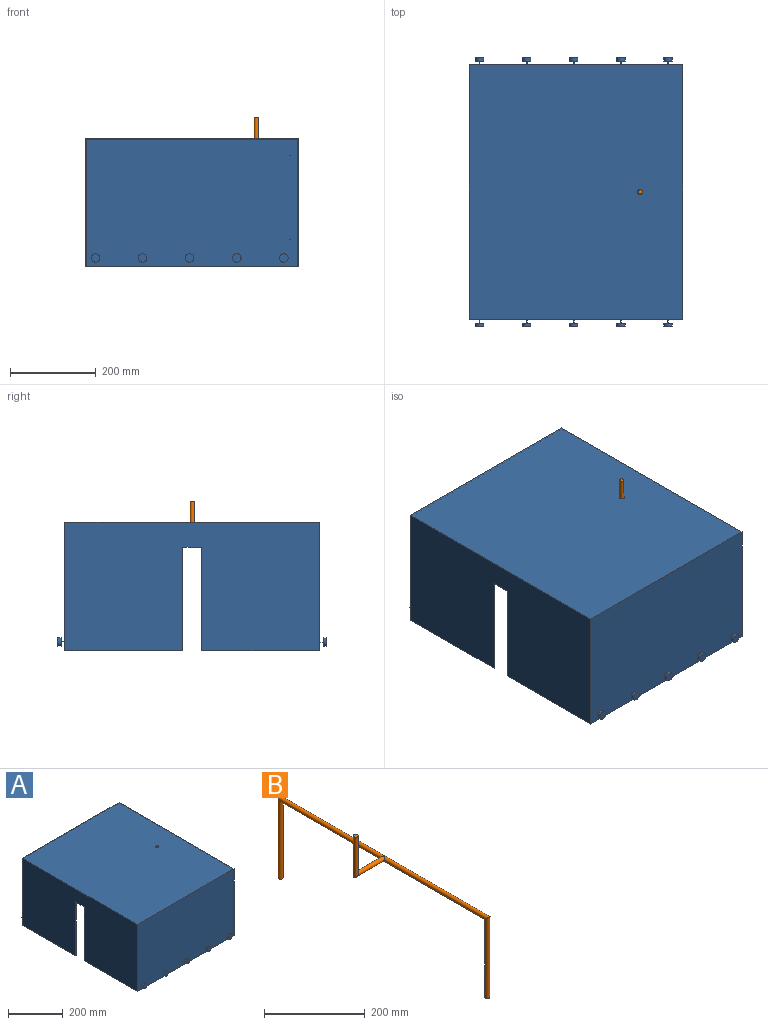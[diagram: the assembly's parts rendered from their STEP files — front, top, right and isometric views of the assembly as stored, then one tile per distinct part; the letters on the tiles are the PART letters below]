
ASSEMBLY  parts=2 mates=1
PART A: 59 faces, bbox 500x628x300 mm
  f0: plane 500x275.5mm, normal (0,0,-1), area 2615mm2, adj f4,f5,f6,f9,f10,f11,f12,f17
  f1: plane 500x275.5mm, normal (0,0,-1), area 2615mm2, adj f2,f5,f6,f7,f10,f11,f14,f15
  f2: plane 500x300mm, normal (0,1,0), area 149984.3mm2, adj f1,f3,f5,f6,f22,f26,f30,f34
  f3: plane 595x500mm, normal (0,0,1), area 297386.9mm2, adj f2,f4,f5,f6,f58
  f4: plane 500x300mm, normal (0,-1,0), area 149984.3mm2, adj f0,f3,f5,f6,f18,f42,f46,f50
  f5: plane 595x300mm, normal (-1,0,0), area 167858.5mm2, adj f0,f1,f2,f3,f4,f15,f16,f17
  f6: plane 595x300mm, normal (1,0,0), area 167858.5mm2, adj f0,f1,f2,f3,f4,f12,f13,f14
  f7: plane 495x297.5mm, normal (0,-1,0), area 147262.5mm2, adj f1,f8,f10,f11
  f8: plane 590x495mm, normal (0,0,-1), area 291936.9mm2, adj f7,f9,f10,f11,f58
  f9: plane 495x297.5mm, normal (0,1,0), area 147262.5mm2, adj f0,f8,f10,f11
  f10: plane 590x297.5mm, normal (1,0,0), area 164883.5mm2, adj f0,f1,f7,f8,f9,f15,f16,f17
  f11: plane 590x297.5mm, normal (-1,0,0), area 164883.5mm2, adj f0,f1,f7,f8,f9,f12,f13,f14
  f12: plane 241.85x2.5mm, normal (0,1,0), area 604.6mm2, adj f0,f6,f11,f13
  f13: plane 44x2.5mm, normal (0,0,-1), area 110mm2, adj f6,f11,f12,f14
  f14: plane 241.85x2.5mm, normal (0,-1,0), area 604.6mm2, adj f1,f6,f11,f13
  f15: plane 241.85x2.5mm, normal (0,-1,0), area 604.6mm2, adj f1,f5,f10,f16
  f16: plane 44x2.5mm, normal (0,0,-1), area 110mm2, adj f5,f10,f15,f17
  f17: plane 241.85x2.5mm, normal (0,1,0), area 604.6mm2, adj f0,f5,f10,f16
  f18: cylinder r=1mm len=9mm, axis (0,1,0), area 56.5mm2, adj f4,f21
  f19: cylinder r=10mm len=20mm, axis (0,1,0), area 439.8mm2, adj f20,f21
  f20: plane 20x20mm, normal (0,-1,0), area 314.2mm2, adj f19
  f21: plane 20x20mm, normal (0,1,0), area 311mm2, adj f18,f19
  f22: cylinder r=1mm len=9mm, axis (0,-1,0), area 56.5mm2, adj f2,f25
  f23: cylinder r=10mm len=20mm, axis (0,-1,0), area 502.7mm2, adj f24,f25
  f24: plane 20x20mm, normal (0,1,0), area 314.2mm2, adj f23
  f25: plane 20x20mm, normal (0,-1,0), area 311mm2, adj f22,f23
  f26: cylinder r=1mm len=9mm, axis (0,-1,0), area 56.5mm2, adj f2,f29
  f27: cylinder r=10mm len=20mm, axis (0,-1,0), area 502.7mm2, adj f28,f29
  f28: plane 20x20mm, normal (0,1,0), area 314.2mm2, adj f27
  f29: plane 20x20mm, normal (0,-1,0), area 311mm2, adj f26,f27
  f30: cylinder r=1mm len=9mm, axis (0,-1,0), area 56.5mm2, adj f2,f33
  f31: cylinder r=10mm len=20mm, axis (0,-1,0), area 502.7mm2, adj f32,f33
  f32: plane 20x20mm, normal (0,1,0), area 314.2mm2, adj f31
  f33: plane 20x20mm, normal (0,-1,0), area 311mm2, adj f30,f31
  f34: cylinder r=1mm len=9mm, axis (0,-1,0), area 56.5mm2, adj f2,f37
  f35: cylinder r=10mm len=20mm, axis (0,-1,0), area 502.7mm2, adj f36,f37
  f36: plane 20x20mm, normal (0,1,0), area 314.2mm2, adj f35
  f37: plane 20x20mm, normal (0,-1,0), area 311mm2, adj f34,f35
  f38: cylinder r=1mm len=9mm, axis (0,-1,0), area 56.5mm2, adj f2,f41
  f39: cylinder r=10mm len=20mm, axis (0,-1,0), area 502.7mm2, adj f40,f41
  f40: plane 20x20mm, normal (0,1,0), area 314.2mm2, adj f39
  f41: plane 20x20mm, normal (0,-1,0), area 311mm2, adj f38,f39
  f42: cylinder r=1mm len=9mm, axis (0,1,0), area 56.5mm2, adj f4,f45
  f43: cylinder r=10mm len=20mm, axis (0,1,0), area 439.8mm2, adj f44,f45
  f44: plane 20x20mm, normal (0,-1,0), area 314.2mm2, adj f43
  f45: plane 20x20mm, normal (0,1,0), area 311mm2, adj f42,f43
  f46: cylinder r=1mm len=9mm, axis (0,1,0), area 56.5mm2, adj f4,f49
  f47: cylinder r=10mm len=20mm, axis (0,1,0), area 439.8mm2, adj f48,f49
  f48: plane 20x20mm, normal (0,-1,0), area 314.2mm2, adj f47
  f49: plane 20x20mm, normal (0,1,0), area 311mm2, adj f46,f47
  f50: cylinder r=1mm len=9mm, axis (0,1,0), area 56.5mm2, adj f4,f53
  f51: cylinder r=10mm len=20mm, axis (0,1,0), area 439.8mm2, adj f52,f53
  f52: plane 20x20mm, normal (0,-1,0), area 314.2mm2, adj f51
  f53: plane 20x20mm, normal (0,1,0), area 311mm2, adj f50,f51
  f54: cylinder r=1mm len=9mm, axis (0,1,0), area 56.5mm2, adj f4,f57
  f55: cylinder r=10mm len=20mm, axis (0,1,0), area 439.8mm2, adj f56,f57
  f56: plane 20x20mm, normal (0,-1,0), area 314.2mm2, adj f55
  f57: plane 20x20mm, normal (0,1,0), area 311mm2, adj f54,f55
  f58: cylinder r=6mm len=12mm, axis (0,0,1), area 94.2mm2, adj f3,f8
PART B: 9 faces, bbox 88.7x590.7x286.5 mm
  f0: cylinder r=5mm len=590.71mm, axis (0,1,0), area 18143.4mm2, adj f3,f4,f5,f7
  f1: plane 10x10mm, normal (0,0,-1), area 78.5mm2, adj f3
  f2: plane 10x10mm, normal (0,0,-1), area 78.5mm2, adj f4
  f3: cylinder r=5mm len=197.85mm, axis (0,0,-1), area 6058.6mm2, adj f0,f1
  f4: cylinder r=5mm len=197.85mm, axis (0,0,1), area 6058.6mm2, adj f0,f2
  f5: plane 2.52x0.16mm, normal (1,0,0), area 0.3mm2, adj f0,f7
  f6: plane 10x10mm, normal (0,0,1), area 78.5mm2, adj f8
  f7: cylinder r=5mm len=83.68mm, axis (1,0,0), area 2371.8mm2, adj f0,f5,f8
  f8: cylinder r=5mm len=98.54mm, axis (0,0,-1), area 2938.4mm2, adj f6,f7
PLACE A at identity fixed
PLACE B t=(-21.32,0,-36.98)mm
MATE fastened B.f8 <-> A.f58  axis (0,0,-1) through (-100,0,480)mm
